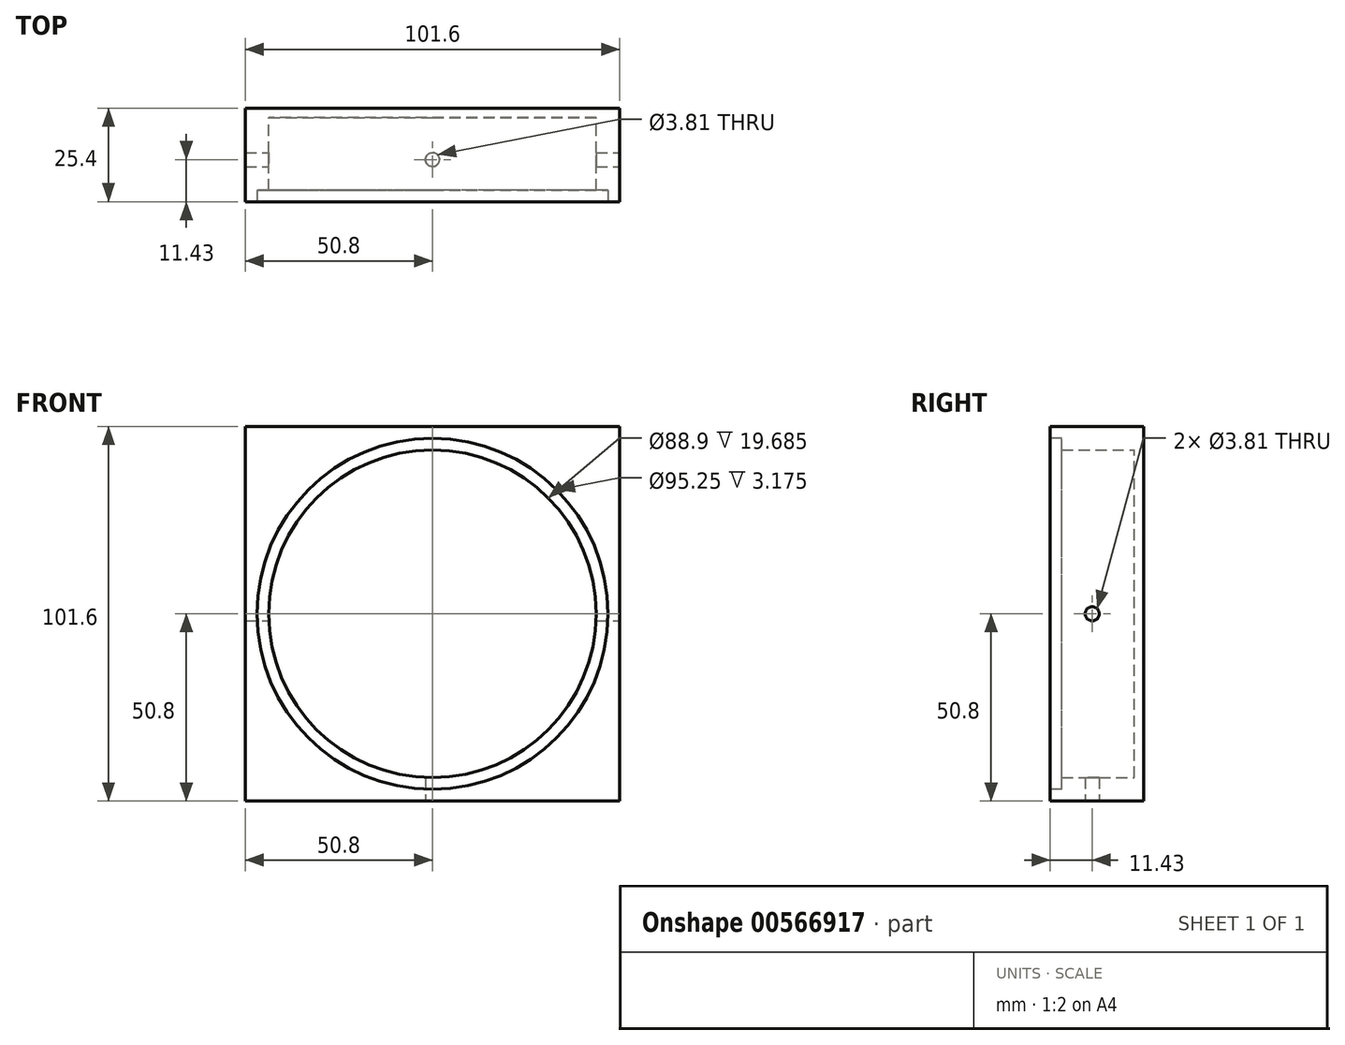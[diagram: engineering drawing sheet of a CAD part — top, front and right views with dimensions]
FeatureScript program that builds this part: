
annotation { "Feature Type Name" : "Feature", "Feature Type Description" : "" }
export const myFeature = defineFeature(function(context is Context, id is Id, definition is map)
    precondition{}
    {
        {
            var Q0;
            Q0=qCreatedBy(makeId("Front.planeOp"),FACE);
            var sketch = newSketch(context, id + "F0", { "sketchPlane" : qUnion([Q0])});
            skLineSegment(sketch, "E0.bottom", {"start": v(-50.8, 50.8) * mm, "end": v(50.8, 50.8) * mm});
            skLineSegment(sketch, "E0.top", {"start": v(-50.8, -50.8) * mm, "end": v(50.8, -50.8) * mm});
            skLineSegment(sketch, "E0.left", {"start": v(-50.8, 50.8) * mm, "end": v(-50.8, -50.8) * mm});
            skLineSegment(sketch, "E0.right", {"start": v(50.8, 50.8) * mm, "end": v(50.8, -50.8) * mm});
            skPoint(sketch, "E0.middle", {"position": v(0, 0) * mm});
            skCircle(sketch, "E1", {"center": v(0, 0) * mm, "radius": 44.45 * mm});
            skCircle(sketch, "E2", {"center": v(0, 0) * mm, "radius": 41.91 * mm});
            skSolve(sketch);
        }
        {
            var Q0;
            Q0=makeQuery(id+"F0.imprint","IMPRINT",FACE,{"disambiguationData":[TD([[makeQuery(id+"F0.imprint","IMPRINT",EDGE,{"derivedFrom":sQuery(id+"F0.wireOp",EDGE,"E0.bottom")}),-1.0]])]});
            extrude(context, id + "F1", {"entities" : qUnion([Q0]), "depth" : 22.86 * mm, "offsetDistance" : 25.4 * mm});
        }
        {
            var Q0;
            Q0=makeQuery(id+"F1.opExtrude","SWEPT_FACE",FACE,{"disambiguationData":[OSD([sQuery(id+"F0.wireOp",EDGE,"E0.top")])]});
            var sketch = newSketch(context, id + "F2", { "sketchPlane" : qUnion([Q0])});
            skCircle(sketch, "E3", {"center": v(0, 11.43) * mm, "radius": 1.9 * mm});
            skSolve(sketch);
        }
        {
            var Q0;
            Q0=makeQuery(id+"F1.opExtrude","SWEPT_FACE",FACE,{"disambiguationData":[OSD([sQuery(id+"F0.wireOp",EDGE,"E0.right")])]});
            var sketch = newSketch(context, id + "F3", { "sketchPlane" : qUnion([Q0])});
            skCircle(sketch, "E4", {"center": v(-11.43, 0) * mm, "radius": 1.9 * mm});
            skSolve(sketch);
        }
        {
            var Q0;
            Q0=makeQuery(id+"F3.imprint","IMPRINT",FACE,{"disambiguationData":[TD([[makeQuery(id+"F3.imprint","IMPRINT",EDGE,{"derivedFrom":sQuery(id+"F3.wireOp",EDGE,"E4")}),1.0]])]});
            extrude(context, id + "F4", {"entities" : qUnion([Q0]), "operationType" : NewBodyOperationType.REMOVE, "endBound" : BoundingType.THROUGH_ALL, "oppositeDirection" : true, "depth" : 6.35 * mm, "offsetDistance" : 25.4 * mm});
        }
        {
            var Q0;
            Q0=makeQuery(id+"F2.imprint","IMPRINT",FACE,{"disambiguationData":[TD([[makeQuery(id+"F2.imprint","IMPRINT",EDGE,{"derivedFrom":sQuery(id+"F2.wireOp",EDGE,"E3")}),1.0]])]});
            extrude(context, id + "F5", {"entities" : qUnion([Q0]), "operationType" : NewBodyOperationType.REMOVE, "endBound" : BoundingType.UP_TO_NEXT, "oppositeDirection" : true, "depth" : 25.4 * mm, "offsetDistance" : 25.4 * mm});
        }
        {
            var Q0;
            Q0=qCreatedBy(makeId("Front.planeOp"),FACE);
            var sketch = newSketch(context, id + "F6", { "sketchPlane" : qUnion([Q0])});
            skLineSegment(sketch, "E5.bottom", {"start": v(-50.8, -50.8) * mm, "end": v(50.8, -50.8) * mm});
            skLineSegment(sketch, "E5.top", {"start": v(-50.8, 50.8) * mm, "end": v(50.8, 50.8) * mm});
            skLineSegment(sketch, "E5.left", {"start": v(-50.8, -50.8) * mm, "end": v(-50.8, 50.8) * mm});
            skLineSegment(sketch, "E5.right", {"start": v(50.8, -50.8) * mm, "end": v(50.8, 50.8) * mm});
            skPoint(sketch, "E5.middle", {"position": v(0, 0) * mm});
            skSolve(sketch);
        }
        {
            var Q0;
            Q0 = qSketchRegion(id + "F6", true);
            extrude(context, id + "F7", {"entities" : qUnion([Q0]), "operationType" : NewBodyOperationType.ADD, "oppositeDirection" : true, "depth" : 2.54 * mm, "offsetDistance" : 25.4 * mm});
        }
        {
            var Q0;
            Q0=makeQuery(id+"F1.opExtrude","CAP_FACE",FACE,{"disambiguationData":[OSD([sQuery(id+"F0.wireOp",EDGE,"E0.bottom"),sQuery(id+"F0.wireOp",EDGE,"E0.top"),sQuery(id+"F0.wireOp",EDGE,"E0.left"),sQuery(id+"F0.wireOp",EDGE,"E0.right"),sQuery(id+"F0.wireOp",EDGE,"E1")])],"isStart":false});
            var sketch = newSketch(context, id + "F8", { "sketchPlane" : qUnion([Q0])});
            skCircle(sketch, "E6", {"center": v(0, 0) * mm, "radius": 47.63 * mm});
            skSolve(sketch);
        }
        {
            var Q0;
            Q0 = qSketchRegion(id + "F8", true);
            extrude(context, id + "F9", {"entities" : qUnion([Q0]), "operationType" : NewBodyOperationType.REMOVE, "oppositeDirection" : true, "depth" : 3.17 * mm, "offsetDistance" : 25.4 * mm});
        }
    });
